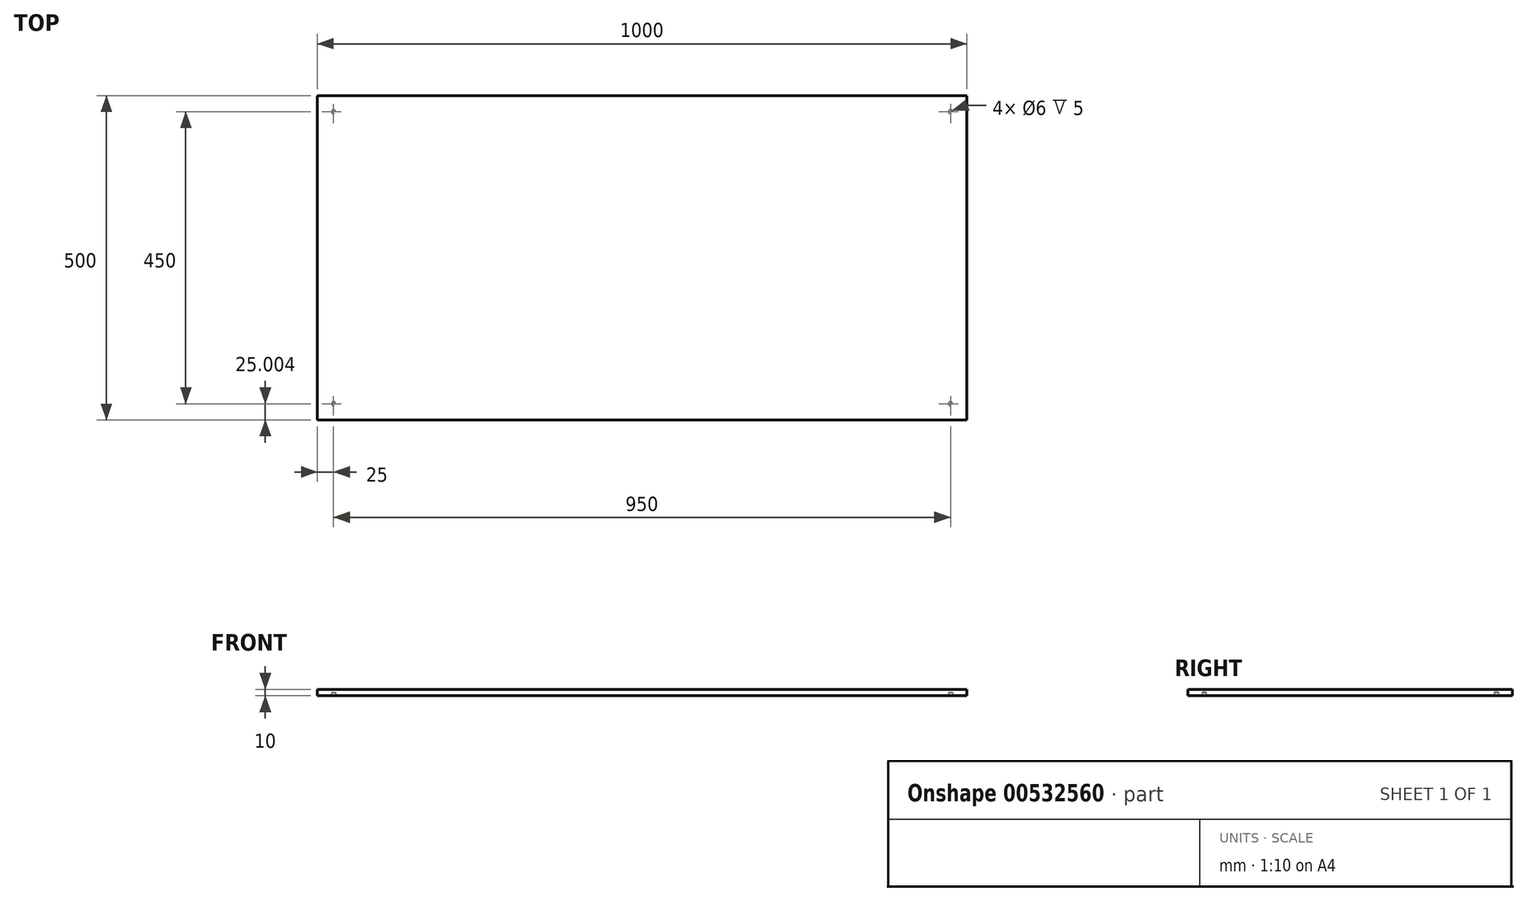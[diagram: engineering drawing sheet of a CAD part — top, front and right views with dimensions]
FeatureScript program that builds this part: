
annotation { "Feature Type Name" : "Feature", "Feature Type Description" : "" }
export const myFeature = defineFeature(function(context is Context, id is Id, definition is map)
    precondition{}
    {
        {
            var Q0;
            Q0=qCreatedBy(makeId("Top.planeOp"),FACE);
            var sketch = newSketch(context, id + "F0", { "sketchPlane" : qUnion([Q0])});
            skLineSegment(sketch, "E0.bottom", {"start": v(0, 1.35) * mm, "end": v(1000, 1.35) * mm});
            skLineSegment(sketch, "E0.top", {"start": v(0, 501.35) * mm, "end": v(1000, 501.35) * mm});
            skLineSegment(sketch, "E0.left", {"start": v(0, 1.35) * mm, "end": v(0, 501.35) * mm});
            skLineSegment(sketch, "E0.right", {"start": v(1000, 1.35) * mm, "end": v(1000, 501.35) * mm});
            skSolve(sketch);
        }
        {
            var Q0;
            Q0 = qSketchRegion(id + "F0", true);
            extrude(context, id + "F1", {"entities" : qUnion([Q0]), "depth" : 10 * mm, "offsetDistance" : 25 * mm});
        }
        {
            var Q0;
            Q0=makeQuery(id+"F1.opExtrude","CAP_FACE",FACE,{"disambiguationData":[OSD([sQuery(id+"F0.wireOp",EDGE,"E0.bottom"),sQuery(id+"F0.wireOp",EDGE,"E0.top"),sQuery(id+"F0.wireOp",EDGE,"E0.left"),sQuery(id+"F0.wireOp",EDGE,"E0.right")])],"isStart":true});
            var sketch = newSketch(context, id + "F2", { "sketchPlane" : qUnion([Q0])});
            skCircle(sketch, "E1", {"center": v(25, -26.35) * mm, "radius": 3 * mm});
            skCircle(sketch, "E2", {"center": v(25, -476.35) * mm, "radius": 3 * mm});
            skCircle(sketch, "E3", {"center": v(975, -26.35) * mm, "radius": 3 * mm});
            skCircle(sketch, "E4", {"center": v(975, -476.35) * mm, "radius": 3 * mm});
            skSolve(sketch);
        }
        {
            var Q0;
            Q0=makeQuery(id+"F2.imprint","IMPRINT",FACE,{"disambiguationData":[TD([[makeQuery(id+"F2.imprint","IMPRINT",EDGE,{"derivedFrom":sQuery(id+"F2.wireOp",EDGE,"E1")}),1.0]])]});
            extrude(context, id + "F3", {"entities" : qUnion([Q0]), "operationType" : NewBodyOperationType.REMOVE, "oppositeDirection" : true, "depth" : 5 * mm, "offsetDistance" : 25 * mm});
        }
        {
            var Q0;
            Q0=makeQuery(id+"F2.imprint","IMPRINT",FACE,{"disambiguationData":[TD([[makeQuery(id+"F2.imprint","IMPRINT",EDGE,{"derivedFrom":sQuery(id+"F2.wireOp",EDGE,"E2")}),1.0]])]});
            extrude(context, id + "F4", {"entities" : qUnion([Q0]), "operationType" : NewBodyOperationType.REMOVE, "oppositeDirection" : true, "depth" : 5 * mm, "offsetDistance" : 25 * mm});
        }
        {
            var Q0;
            Q0 = qSketchRegion(id + "F2", true);
            extrude(context, id + "F5", {"entities" : qUnion([Q0]), "operationType" : NewBodyOperationType.REMOVE, "oppositeDirection" : true, "depth" : 5 * mm, "offsetDistance" : 25 * mm});
        }
    });
